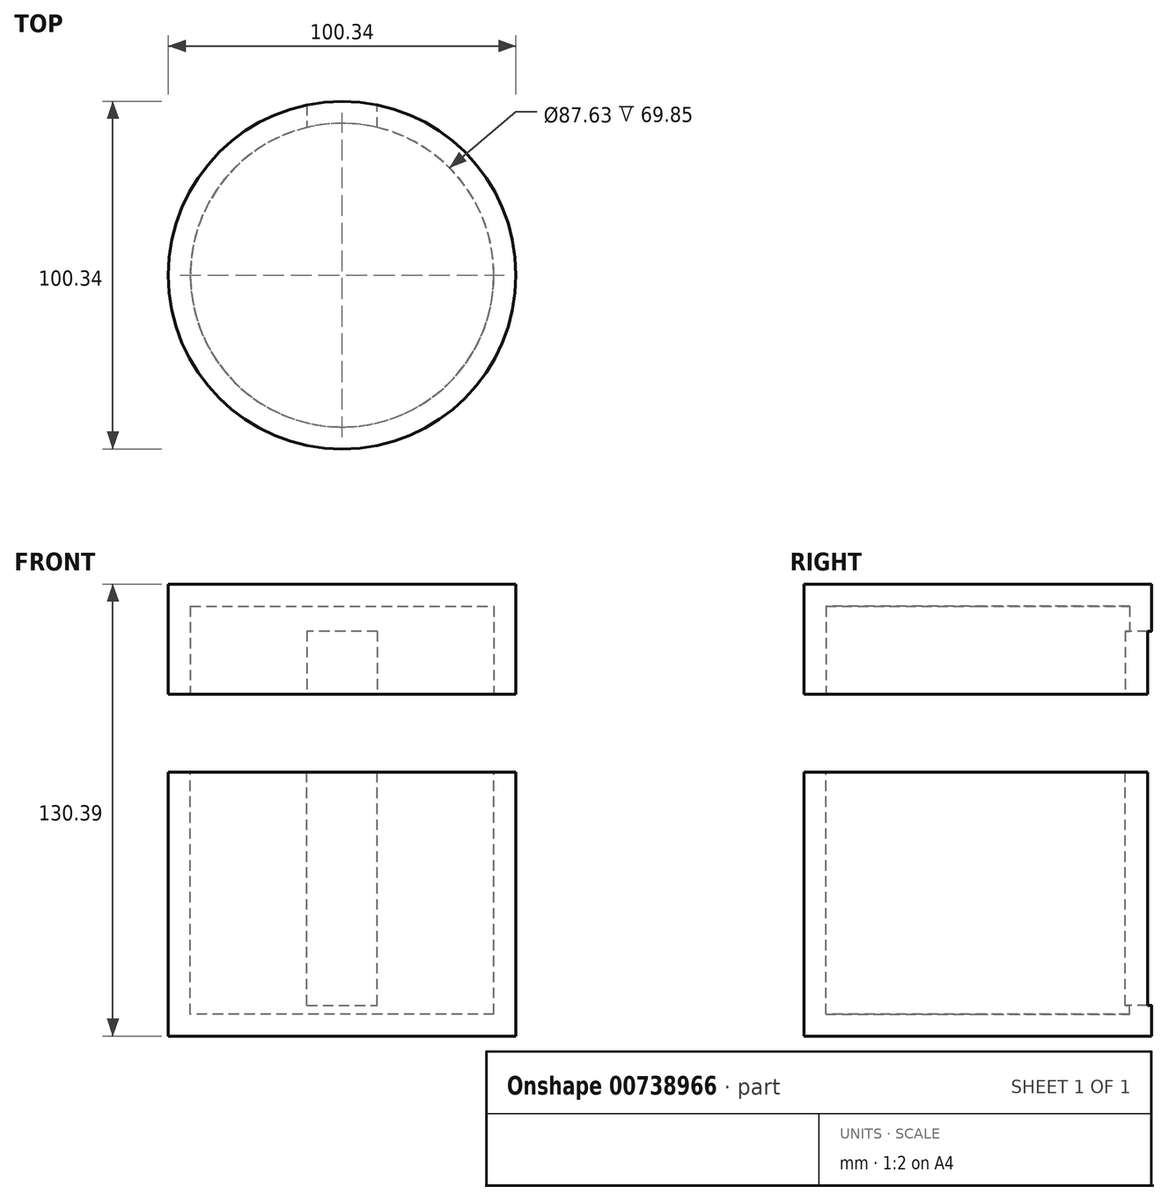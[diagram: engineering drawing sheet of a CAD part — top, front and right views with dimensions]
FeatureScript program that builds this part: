
annotation { "Feature Type Name" : "Feature", "Feature Type Description" : "" }
export const myFeature = defineFeature(function(context is Context, id is Id, definition is map)
    precondition{}
    {
        {
            var Q0;
            Q0=qCreatedBy(makeId("Front.planeOp"),FACE);
            var sketch = newSketch(context, id + "F0", { "sketchPlane" : qUnion([Q0])});
            skLineSegment(sketch, "E0", {"start": v(0, 0) * mm, "end": v(50.16, 0) * mm});
            skLineSegment(sketch, "E1", {"start": v(50.17, 0) * mm, "end": v(50.17, 76.2) * mm});
            skLineSegment(sketch, "E2", {"start": v(50.17, 76.2) * mm, "end": v(43.81, 76.2) * mm});
            skLineSegment(sketch, "E3", {"start": v(43.81, 76.2) * mm, "end": v(43.82, 6.35) * mm});
            skLineSegment(sketch, "E4", {"start": v(43.82, 6.35) * mm, "end": v(0, 6.35) * mm});
            skLineSegment(sketch, "E5", {"start": v(0, 6.35) * mm, "end": v(0, 0) * mm});
            skSolve(sketch);
        }
        {
            var Q0;
            Q0 = qSketchRegion(id + "F0", true);
            var Q1;
            Q1=sQuery(id+"F0.wireOp",EDGE,"E5");
            revolve(context, id + "F1", {"surfaceOperationType" : NewSurfaceOperationType.NEW, "entities" : qUnion([Q0]), "axis" : qUnion([Q1]), "revolveType" : RevolveType.FULL});
        }
        {
            var Q0;
            Q0=qCreatedBy(makeId("Front.planeOp"),FACE);
            var sketch = newSketch(context, id + "F2", { "sketchPlane" : qUnion([Q0])});
            skLineSegment(sketch, "E6", {"start": v(0, 0) * mm, "end": v(0, 8.9) * mm});
            skLineSegment(sketch, "E7", {"start": v(0, 8.9) * mm, "end": v(10.16, 8.9) * mm});
            skLineSegment(sketch, "E8", {"start": v(10.16, 8.9) * mm, "end": v(10.16, 76.2) * mm});
            skLineSegment(sketch, "E9", {"start": v(10.16, 76.2) * mm, "end": v(-10.16, 76.2) * mm});
            skLineSegment(sketch, "E10", {"start": v(-10.16, 76.2) * mm, "end": v(-10.16, 8.9) * mm});
            skLineSegment(sketch, "E11", {"start": v(-10.16, 8.9) * mm, "end": v(0, 8.9) * mm});
            skSolve(sketch);
        }
        {
            var Q0;
            Q0=makeQuery(id+"F2.imprint","IMPRINT",FACE,{"disambiguationData":[TD([[makeQuery(id+"F2.imprint","IMPRINT",EDGE,{"derivedFrom":sQuery(id+"F2.wireOp",EDGE,"E7")}),1.0]])]});
            extrude(context, id + "F3", {"entities" : qUnion([Q0]), "operationType" : NewBodyOperationType.REMOVE, "oppositeDirection" : true, "depth" : 99.06 * mm, "offsetDistance" : 25.4 * mm});
        }
        {
            var Q0;
            Q0=qCreatedBy(makeId("Front.planeOp"),FACE);
            var sketch = newSketch(context, id + "F4", { "sketchPlane" : qUnion([Q0])});
            skLineSegment(sketch, "E12", {"start": v(0, 130.39) * mm, "end": v(50.16, 130.39) * mm});
            skLineSegment(sketch, "E13", {"start": v(50.16, 130.39) * mm, "end": v(50.16, 98.64) * mm});
            skLineSegment(sketch, "E14", {"start": v(50.16, 98.64) * mm, "end": v(43.81, 98.64) * mm});
            skLineSegment(sketch, "E15", {"start": v(43.81, 98.64) * mm, "end": v(43.81, 124.04) * mm});
            skLineSegment(sketch, "E16", {"start": v(43.81, 124.04) * mm, "end": v(0, 124.04) * mm});
            skLineSegment(sketch, "E17", {"start": v(0, 124.04) * mm, "end": v(0, 130.39) * mm});
            skSolve(sketch);
        }
        {
            var Q0;
            Q0=makeQuery(id+"F4.imprint","IMPRINT",FACE,{"disambiguationData":[TD([[makeQuery(id+"F4.imprint","IMPRINT",EDGE,{"derivedFrom":sQuery(id+"F4.wireOp",EDGE,"E12")}),-1.0]])]});
            var Q1;
            Q1=sQuery(id+"F4.wireOp",EDGE,"E17");
            revolve(context, id + "F5", {"surfaceOperationType" : NewSurfaceOperationType.NEW, "entities" : qUnion([Q0]), "axis" : qUnion([Q1]), "revolveType" : RevolveType.FULL});
        }
        {
            var Q0;
            Q0=qCreatedBy(makeId("Front.planeOp"),FACE);
            var sketch = newSketch(context, id + "F6", { "sketchPlane" : qUnion([Q0])});
            skLineSegment(sketch, "E18", {"start": v(0, 78.74) * mm, "end": v(10.16, 78.74) * mm});
            skLineSegment(sketch, "E19", {"start": v(10.16, 78.74) * mm, "end": v(10.16, 116.84) * mm});
            skLineSegment(sketch, "E20", {"start": v(10.16, 116.84) * mm, "end": v(-10.16, 116.84) * mm});
            skLineSegment(sketch, "E21", {"start": v(-10.16, 116.84) * mm, "end": v(-10.16, 78.74) * mm});
            skLineSegment(sketch, "E22", {"start": v(-10.16, 78.74) * mm, "end": v(0, 78.74) * mm});
            skSolve(sketch);
        }
        {
            var Q0;
            Q0=makeQuery(id+"F6.imprint","IMPRINT",FACE,{"disambiguationData":[TD([[makeQuery(id+"F6.imprint","IMPRINT",EDGE,{"derivedFrom":sQuery(id+"F6.wireOp",EDGE,"E18")}),1.0]])]});
            extrude(context, id + "F7", {"entities" : qUnion([Q0]), "operationType" : NewBodyOperationType.REMOVE, "oppositeDirection" : true, "depth" : 95 * mm, "offsetDistance" : 25.4 * mm});
        }
    });
